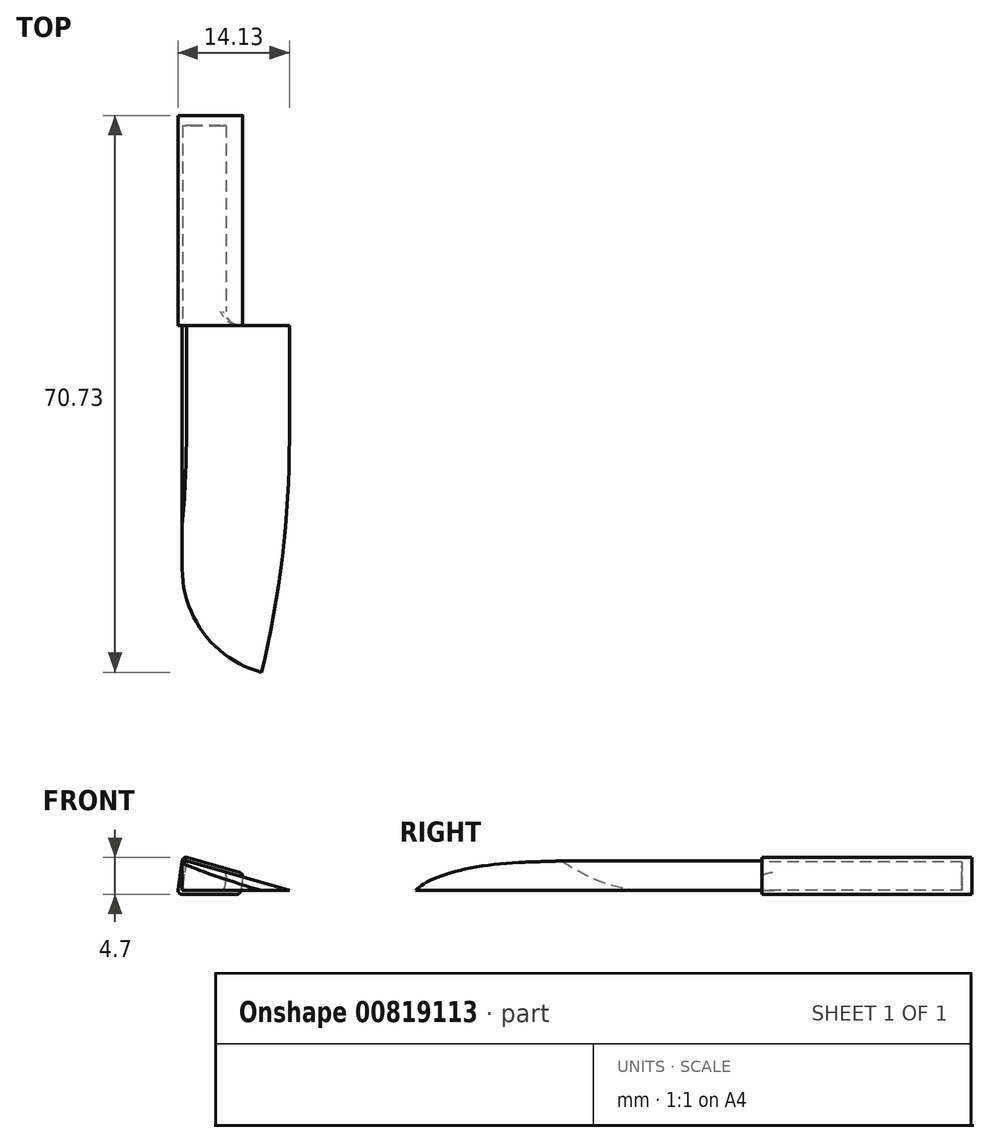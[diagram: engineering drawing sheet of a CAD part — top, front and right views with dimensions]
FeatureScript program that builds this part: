
annotation { "Feature Type Name" : "Feature", "Feature Type Description" : "" }
export const myFeature = defineFeature(function(context is Context, id is Id, definition is map)
    precondition{}
    {
        {
            var Q0;
            Q0=qCreatedBy(makeId("Top.planeOp"),FACE);
            var sketch = newSketch(context, id + "F0", { "sketchPlane" : qUnion([Q0])});
            skLineSegment(sketch, "E0", {"start": v(0, 0) * mm, "end": v(-13.62, 0) * mm});
            skLineSegment(sketch, "E1", {"start": v(0, 0) * mm, "end": v(0, -14.38) * mm});
            skArc(sketch, "E2", {"start": v(-3.52, -44.06) * mm, "mid": v(-0.88, -29.32) * mm, "end": v(0, -14.38) * mm});
            skLineSegment(sketch, "E3", {"start": v(0, 0) * mm, "end": v(-151.3, 0) * mm, "construction": true});
            skLineSegment(sketch, "E4", {"start": v(-126.93, -14.38) * mm, "end": v(-126.93, 0) * mm, "construction": true});
            skLineSegment(sketch, "E5", {"start": v(0, 0) * mm, "end": v(0, -52.32) * mm, "construction": true});
            skLineSegment(sketch, "E6", {"start": v(-3.82, -34.27) * mm, "end": v(0, -34.27) * mm, "construction": true});
            skSolve(sketch);
        }
        {
            var Q0;
            Q0=qCreatedBy(makeId("Front.planeOp"),FACE);
            var sketch = newSketch(context, id + "F1", { "sketchPlane" : qUnion([Q0])});
            skLineSegment(sketch, "E7", {"start": v(0, 0) * mm, "end": v(-13.08, 3.77) * mm});
            skLineSegment(sketch, "E8", {"start": v(-13.08, 3.77) * mm, "end": v(-13.62, 0) * mm});
            skLineSegment(sketch, "E9", {"start": v(-13.62, 0) * mm, "end": v(0, 0) * mm});
            skSolve(sketch);
        }
        {
            var Q0;
            Q0=makeQuery(id+"F1.imprint","IMPRINT",FACE,{"disambiguationData":[TD([[makeQuery(id+"F1.imprint","IMPRINT",EDGE,{"derivedFrom":sQuery(id+"F1.wireOp",EDGE,"E7")}),1.0]])]});
            var Q1;
            Q1=sQuery(id+"F0.wireOp",EDGE,"E1");
            var Q2;
            Q2=sQuery(id+"F0.wireOp",EDGE,"E2");
            sweep(context, id + "F2", {"profiles" : qUnion([Q0]), "path" : qUnion([Q1, Q2])});
        }
        {
            var Q0;
            Q0=qCreatedBy(makeId("Top.planeOp"),FACE);
            var sketch = newSketch(context, id + "F3", { "sketchPlane" : qUnion([Q0])});
            skLineSegment(sketch, "E10", {"start": v(-13.62, 0) * mm, "end": v(-13.62, -30.9) * mm});
            skArc(sketch, "E11", {"start": v(-13.62, -30.9) * mm, "mid": v(-10.8, -39.2) * mm, "end": v(-3.52, -44.06) * mm});
            skLineSegment(sketch, "E12", {"start": v(-3.52, -44.06) * mm, "end": v(-33.26, -48.7) * mm});
            skLineSegment(sketch, "E13", {"start": v(-33.26, -48.7) * mm, "end": v(-13.62, 0) * mm});
            skSolve(sketch);
        }
        {
            var Q0;
            Q0 = qSketchRegion(id + "F3", true);
            extrude(context, id + "F4", {"entities" : qUnion([Q0]), "operationType" : NewBodyOperationType.REMOVE, "depth" : 25.4 * mm, "offsetDistance" : 25.4 * mm});
        }
        {
            var Q0;
            Q0=qCreatedBy(makeId("Front.planeOp"),FACE);
            var sketch = newSketch(context, id + "F5", { "sketchPlane" : qUnion([Q0])});
            skLineSegment(sketch, "E14", {"start": v(-13.62, 0) * mm, "end": v(-13.08, 3.77) * mm});
            skLineSegment(sketch, "E15", {"start": v(-13.08, 3.77) * mm, "end": v(-7.96, 2.3) * mm});
            skLineSegment(sketch, "E16", {"start": v(-7.96, 2.3) * mm, "end": v(-8.28, 0) * mm});
            skLineSegment(sketch, "E17", {"start": v(-8.28, 0) * mm, "end": v(-13.62, 0) * mm});
            skSolve(sketch);
        }
        {
            var Q0;
            Q0 = qSketchRegion(id + "F5", true);
            extrude(context, id + "F6", {"entities" : qUnion([Q0]), "oppositeDirection" : true, "depth" : 25.4 * mm, "offsetDistance" : 25.4 * mm, "hasSecondDirection" : true, "secondDirectionOppositeDirection" : false, "secondDirectionDepth" : 0.03 * mm});
        }
        {
            var Q0;
            Q0=makeQuery(id+"F6.opExtrude","SWEPT_EDGE",EDGE,{"disambiguationData":[OSD([sQuery(id+"F5.wireOp",EDGE,"E15"),sQuery(id+"F5.wireOp",EDGE,"E16")])]});
            var Q1;
            Q1=makeQuery(id+"F6.opExtrude","SWEPT_EDGE",EDGE,{"disambiguationData":[OSD([sQuery(id+"F5.wireOp",EDGE,"E14"),sQuery(id+"F5.wireOp",EDGE,"E15")])]});
            var Q2;
            Q2=makeQuery(id+"F6.opExtrude","SWEPT_EDGE",EDGE,{"disambiguationData":[OSD([sQuery(id+"F5.wireOp",EDGE,"E14"),sQuery(id+"F5.wireOp",EDGE,"E17")])]});
            var Q3;
            Q3=makeQuery(id+"F6.opExtrude","SWEPT_EDGE",EDGE,{"disambiguationData":[OSD([sQuery(id+"F5.wireOp",EDGE,"E16"),sQuery(id+"F5.wireOp",EDGE,"E17")])]});
            fillet(context, id + "F7", {"entities" : qUnion([Q0, Q1, Q2, Q3]), "radius" : 0.5 * mm, "tangentPropagation" : true, "allowEdgeOverflow" : false});
        }
        {
            var Q0;
            Q0=makeQuery(id+"F2.opSweep","SWEPT_BODY",BODY,{"disambiguationData":[OSD([sQuery(id+"F0.wireOp",EDGE,"E2"),sQuery(id+"F1.wireOp",EDGE,"E7"),sQuery(id+"F1.wireOp",EDGE,"E8"),sQuery(id+"F1.wireOp",EDGE,"E9")])]});
            var Q1;
            Q1=makeQuery(id+"F6.opExtrude","SWEPT_BODY",BODY,{"disambiguationData":[OSD([sQuery(id+"F5.wireOp",EDGE,"E14"),sQuery(id+"F5.wireOp",EDGE,"E15"),sQuery(id+"F5.wireOp",EDGE,"E16"),sQuery(id+"F5.wireOp",EDGE,"E17")])]});
            booleanBodies(context, id + "F8", {"operationType" : BooleanOperationType.UNION, "tools" : qUnion([Q0, Q1])});
        }
        {
            var Q0;
            Q0=makeQuery(id+"F8.opBoolean","INTERSECT",EDGE,{"derivedFrom":[makeQuery(id+"F2.opSweep","CAP_FACE",FACE,{"disambiguationData":[OSD([sQuery(id+"F0.wireOp",VERTEX,"E1.start"),sQuery(id+"F1.wireOp",EDGE,"E7"),sQuery(id+"F1.wireOp",EDGE,"E8"),sQuery(id+"F1.wireOp",EDGE,"E9")])],"isStart":true}),makeQuery(id+"F6.opExtrude","SWEPT_FACE",FACE,{"disambiguationData":[OSD([sQuery(id+"F5.wireOp",EDGE,"E16")])]})]});
            fillet(context, id + "F9", {"entities" : qUnion([Q0]), "radius" : 1.78 * mm, "tangentPropagation" : true, "allowEdgeOverflow" : false});
        }
        {
            var Q0;
            Q0=qCreatedBy(makeId("Front.planeOp"),FACE);
            var sketch = newSketch(context, id + "F10", { "sketchPlane" : qUnion([Q0])});
            skLineSegment(sketch, "E18.bottom", {"start": v(-13.52, 4.38) * mm, "end": v(-5.87, 2.17) * mm});
            skLineSegment(sketch, "E18.top", {"start": v(-14.2, -0.47) * mm, "end": v(-6.24, -0.47) * mm});
            skLineSegment(sketch, "E18.left", {"start": v(-13.52, 4.38) * mm, "end": v(-14.2, -0.47) * mm});
            skLineSegment(sketch, "E18.right", {"start": v(-5.87, 2.17) * mm, "end": v(-6.24, -0.47) * mm});
            skSolve(sketch);
        }
        {
            var Q0;
            Q0 = qSketchRegion(id + "F10", true);
            extrude(context, id + "F11", {"entities" : qUnion([Q0]), "oppositeDirection" : true, "depth" : 26.67 * mm, "offsetDistance" : 25.4 * mm});
        }
        {
            var Q0;
            Q0=makeQuery(id+"F2.opSweep","SWEPT_BODY",BODY,{"disambiguationData":[OSD([sQuery(id+"F0.wireOp",EDGE,"E2"),sQuery(id+"F1.wireOp",EDGE,"E7"),sQuery(id+"F1.wireOp",EDGE,"E8"),sQuery(id+"F1.wireOp",EDGE,"E9")])]});
            var Q1;
            Q1=makeQuery(id+"F11.opExtrude","SWEPT_BODY",BODY,{"disambiguationData":[OSD([sQuery(id+"F10.wireOp",EDGE,"E18.bottom"),sQuery(id+"F10.wireOp",EDGE,"E18.top"),sQuery(id+"F10.wireOp",EDGE,"E18.left"),sQuery(id+"F10.wireOp",EDGE,"E18.right")])]});
            booleanBodies(context, id + "F12", {"operationType" : BooleanOperationType.SUBTRACTION, "tools" : qUnion([Q0]), "targets" : qUnion([Q1]), "keepTools" : true});
        }
        {
            var Q0;
            Q0=makeQuery(id+"F11.opExtrude","SWEPT_EDGE",EDGE,{"disambiguationData":[OSD([sQuery(id+"F10.wireOp",EDGE,"E18.bottom"),sQuery(id+"F10.wireOp",EDGE,"E18.right")])]});
            var Q1;
            Q1=makeQuery(id+"F11.opExtrude","SWEPT_EDGE",EDGE,{"disambiguationData":[OSD([sQuery(id+"F10.wireOp",EDGE,"E18.top"),sQuery(id+"F10.wireOp",EDGE,"E18.right")])]});
            var Q2;
            Q2=makeQuery(id+"F11.opExtrude","SWEPT_EDGE",EDGE,{"disambiguationData":[OSD([sQuery(id+"F10.wireOp",EDGE,"E18.bottom"),sQuery(id+"F10.wireOp",EDGE,"E18.left")])]});
            var Q3;
            Q3=makeQuery(id+"F11.opExtrude","SWEPT_EDGE",EDGE,{"disambiguationData":[OSD([sQuery(id+"F10.wireOp",EDGE,"E18.top"),sQuery(id+"F10.wireOp",EDGE,"E18.left")])]});
            fillet(context, id + "F13", {"entities" : qUnion([Q0, Q1, Q2, Q3]), "radius" : 0.5 * mm, "allowEdgeOverflow" : false});
        }
    });
